# Revit family: Solarstone_Solar_Full_Roof_Landscape_BIPV_module
name_source: partatom
category: Curtain Panels
units: mm (PartAtom-declared; Revit-internal decimal feet)

## family parameters
Always vertical = Yes
Cut with Voids When Loaded = No
OmniClass Number = 23.25.20.14.11.11.17
OmniClass Title = Infill Panels
Shared = No

## types (3) — shared parameters
Analytic Construction = <None>
Brand Url = https://solarstone.com
Date of Publishing = 12.03.2026
Define Thermal Properties by = Schematic Type
Depth = 35 mm
Design Country = Estonia
Edition Number = 1
Manufacturer Country = Estonia
Max Power Current (Impp) = 14 A
Max Power Voltage (Vmpp) = 32 V
Max Reverse Current (IR) = 30 A
Max System Voltage = 1500 V
Open Circuit Voltage (VoC) = 38 V
Overlap = 55 mm  [stored 0.180446 ft]
Panel_Category = BIPV
Product Family = Energy
Product Group = Building Integrated PV Panels
Rated Power Pmax = 430 VA
Requirement = Below 18 degrees of roof slope the system requires additional components to be installed below the sub structure
Short Circuit Voltage (Isc) = 14
Width = 1791 mm

## per-type parameters (varying)
| type | Visible Area |
| KIT-A | 1754 x 1140 mm |
| KIT-B | 1754 x 1190 mm |
| KIT-C | 1754 x 1240 mm |

note: source unit labels omitted for Short Circuit Voltage (Isc) — the stored unit's dimension contradicts the parameter name (converter mislabeling)

note: [stored X ft] marks values corroborated as IEEE doubles in the binary element streams (Revit-internal decimal feet)

## geometry (parser evidence)
native form markers: Sweep x3
no freeform markers — native parametric forms only
